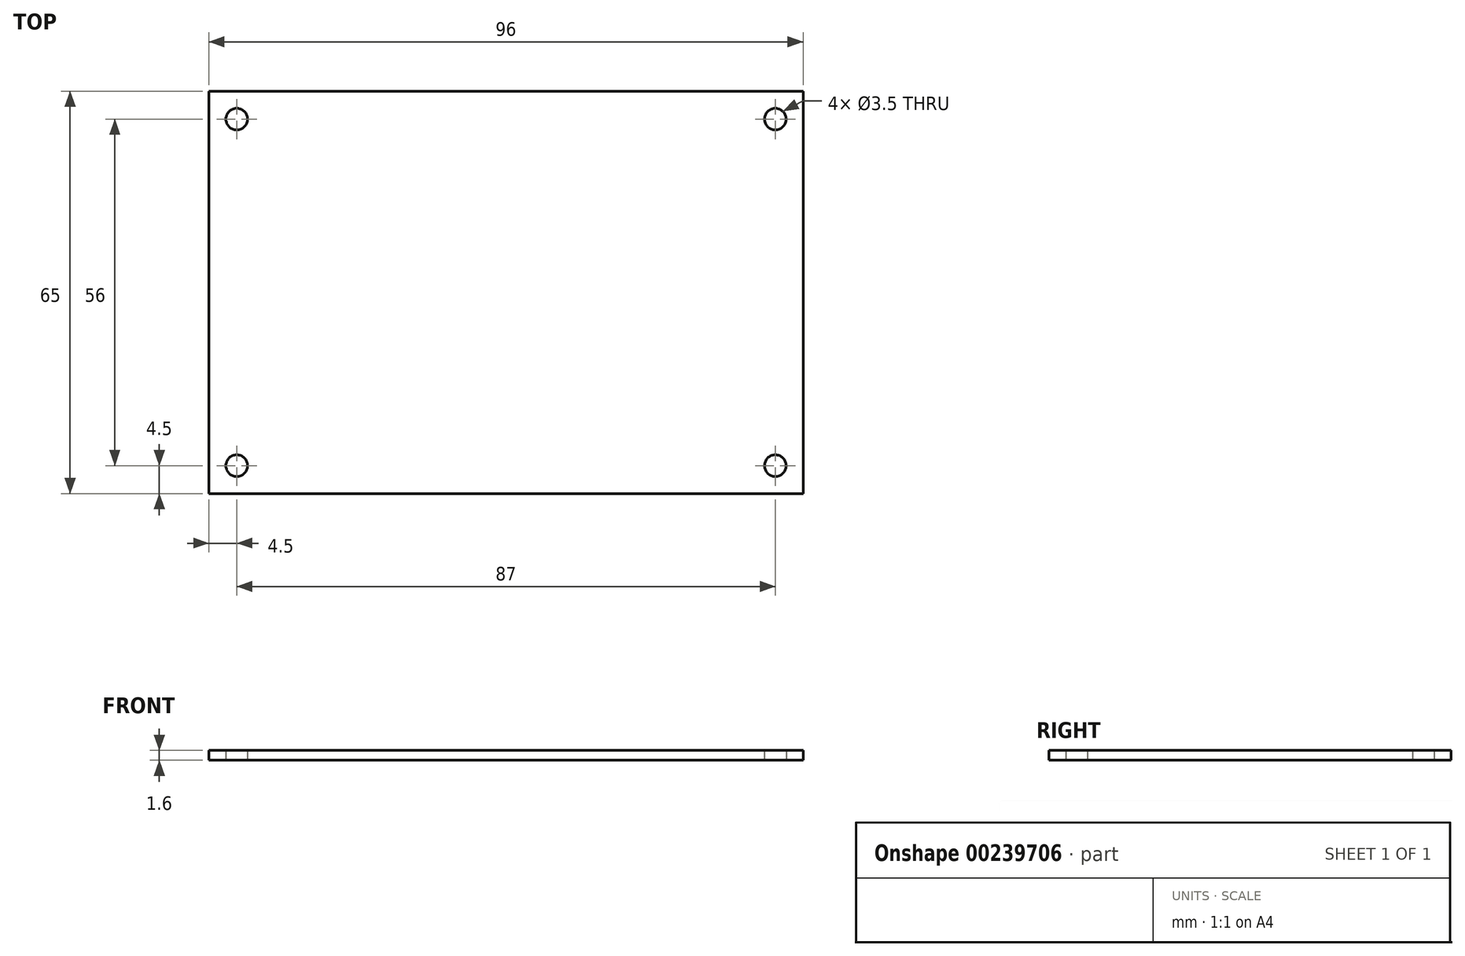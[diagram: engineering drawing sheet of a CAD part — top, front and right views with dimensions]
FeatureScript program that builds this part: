
annotation { "Feature Type Name" : "Feature", "Feature Type Description" : "" }
export const myFeature = defineFeature(function(context is Context, id is Id, definition is map)
    precondition{}
    {
        {
            var Q0;
            Q0=qCreatedBy(makeId("Top.planeOp"),FACE);
            var sketch = newSketch(context, id + "F0", { "sketchPlane" : qUnion([Q0])});
            skLineSegment(sketch, "E0.bottom", {"start": v(48, 32.5) * mm, "end": v(-48, 32.5) * mm});
            skLineSegment(sketch, "E0.top", {"start": v(48, -32.5) * mm, "end": v(-48, -32.5) * mm});
            skLineSegment(sketch, "E0.left", {"start": v(48, 32.5) * mm, "end": v(48, -32.5) * mm});
            skLineSegment(sketch, "E0.right", {"start": v(-48, 32.5) * mm, "end": v(-48, -32.5) * mm});
            skPoint(sketch, "E0.middle", {"position": v(0, 0) * mm});
            skCircle(sketch, "E1", {"center": v(-43.5, 28) * mm, "radius": 1.75 * mm});
            skCircle(sketch, "E2.MirrorC", {"center": v(43.5, 28) * mm, "radius": 1.75 * mm});
            skCircle(sketch, "E3.MirrorC", {"center": v(-43.5, -28) * mm, "radius": 1.75 * mm});
            skCircle(sketch, "E4.MirrorC", {"center": v(43.5, -28) * mm, "radius": 1.75 * mm});
            skSolve(sketch);
        }
        {
            var Q0;
            Q0 = qSketchRegion(id + "F0", true);
            extrude(context, id + "F1", {"entities" : qUnion([Q0]), "depth" : 1.6 * mm});
        }
    });
